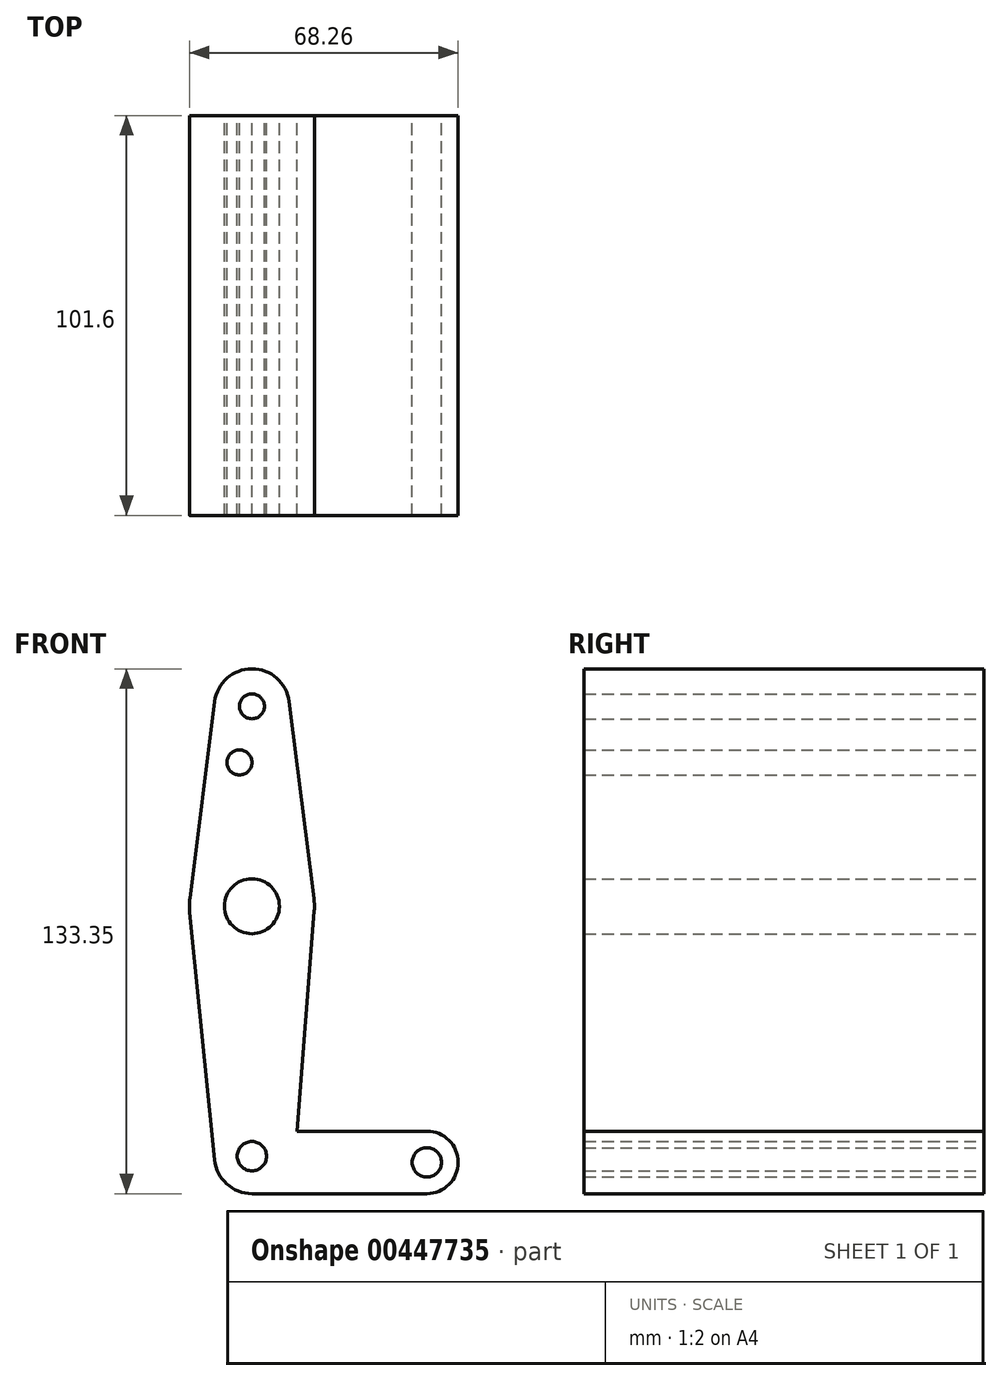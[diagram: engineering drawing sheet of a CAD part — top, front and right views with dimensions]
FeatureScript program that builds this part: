
annotation { "Feature Type Name" : "Feature", "Feature Type Description" : "" }
export const myFeature = defineFeature(function(context is Context, id is Id, definition is map)
    precondition{}
    {
        {
            var Q0;
            Q0=qCreatedBy(makeId("Front.planeOp"),FACE);
            var sketch = newSketch(context, id + "F0", { "sketchPlane" : qUnion([Q0])});
            skCircle(sketch, "E0", {"center": v(0, 0) * mm, "radius": 15.88 * mm});
            skLineSegment(sketch, "E1", {"start": v(-15.75, 1.98) * mm, "end": v(-8.76, 57.5) * mm});
            skLineSegment(sketch, "E2", {"start": v(8.83, 56.9) * mm, "end": v(15.75, 1.98) * mm});
            skLineSegment(sketch, "E3", {"start": v(15.75, 1.98) * mm, "end": v(8.83, 56.9) * mm});
            skCircle(sketch, "E4", {"center": v(0, -63.5) * mm, "radius": 9.53 * mm});
            skCircle(sketch, "E5", {"center": v(44.45, -65.09) * mm, "radius": 7.94 * mm});
            skLineSegment(sketch, "E6", {"start": v(-15.8, -1.59) * mm, "end": v(-9.48, -64.45) * mm});
            skLineSegment(sketch, "E7", {"start": v(0, -73.03) * mm, "end": v(44.45, -73.03) * mm});
            skLineSegment(sketch, "E8", {"start": v(44.45, -57.15) * mm, "end": v(11.46, -57.15) * mm});
            skCircle(sketch, "E9", {"center": v(0, 50.8) * mm, "radius": 3.18 * mm});
            skCircle(sketch, "E10", {"center": v(0, 0) * mm, "radius": 6.98 * mm});
            skCircle(sketch, "E11", {"center": v(44.45, -65.09) * mm, "radius": 3.73 * mm});
            skCircle(sketch, "E12", {"center": v(-3.17, 36.53) * mm, "radius": 3.18 * mm});
            skCircle(sketch, "E13", {"center": v(0, 50.8) * mm, "radius": 9.53 * mm});
            skLineSegment(sketch, "E14", {"start": v(0, 50.8) * mm, "end": v(0, -63.5) * mm, "construction": true});
            skCircle(sketch, "E15", {"center": v(0, -63.5) * mm, "radius": 3.73 * mm});
            skLineSegment(sketch, "E16", {"start": v(11.46, -57.15) * mm, "end": v(15.83, -1.23) * mm});
            skSolve(sketch);
        }
        {
            var Q0;
            Q0 = qSketchRegion(id + "F0", true);
            extrude(context, id + "F1", {"entities" : qUnion([Q0]), "depth" : 101.6 * mm});
        }
    });
